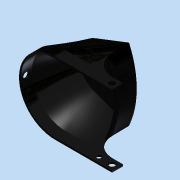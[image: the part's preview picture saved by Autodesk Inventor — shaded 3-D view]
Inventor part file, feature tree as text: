
AUTODESK INVENTOR PART (.ipt)
format: ipt  version: 2015 (Build 190159000, 159)  size: 537,600 bytes
history: native  units: in
note: dims shown in document units (in); Inventor stores cm internally (conversion verified against a paired STEP export)
features: sketch x11, extrude x8, other x4, plane x3, mirror x2, projected_geometry x2, loft x1, sweep x1
ambient origin geometry x8: Origin, YZ Plane, XZ Plane, XY Plane, X Axis, Y Axis, Z Axis, Center Point
bodies: Solid1 (feature_tree)
feature tree (32):
  other  "MotorMount.ipt"
  sketch  "Sketch2"  dims[d0=0.3937in d1=1.3189in]
  sketch  "Sketch3"  dims[d2=1.5748in d3=0.0625in]
  plane  "Work Plane1"
  loft  "Loft1"
  extrude  "Extrusion1"  Depth=0.0625in
  extrude  "Extrusion2"  TaperAngle=0.0deg  [1 undecoded]
  sketch  "Sketch6"  dims[d10=0.0in d11=0.0625in]
  extrude  "Extrusion3"  Depth=0.0625in
  plane  "Work Plane2"
  extrude  "Extrusion4"  Depth=0.0625in
  sketch  "Sketch8"  dims[d14=0.0625in d15=0.0in]
  extrude  "Extrusion5"  TaperAngle=0.0deg  [1 undecoded]
  extrude  "Extrusion6"  TaperAngle=0.0deg  [1 undecoded]
  plane  "Work Plane3"
  mirror  "Mirror1"
  extrude  "Extrusion7"  TaperAngle=0.0deg  [1 undecoded]
  mirror  "Mirror2"
  sketch  "Sketch10"  dims[d18=0.1339in d19=0.1339in]
  sweep  "Sweep2"
  extrude  "Extrusion8"  Depth=0.1339in
  other  "TaggingFeature1"
  sketch  "Sketch4"  dims[d4=0.0625in d5=0.0in d6=90.0deg]
  sketch  "Sketch5"  dims[d7=0.0in d8=90.0deg d9=0.0625in]
  sketch  "Sketch7"  dims[d12=0.0625in d13=0.0in]
  sketch  "Sketch9"  dims[d16=0.0625in d17=0.0in]
  projected_geometry  "Projected Loop1"
  projected_geometry  "Projected Loop2"
  sketch  "Sketch11"  dims[d20=0.1339in d21=0.1339in d22=0.1969in d23=0.1969in d24=0.1969in d25=0.1969in d26=0.1412in d27=0.0in d28=0.0625in d29=0.0in d31=0.75in d32=0.0625in d33=0.0in d34=0.96in d35=0.96in d36=0.0625in d39=0.0in d40=0.0in d41=0.5in d42=0.0in d44=0.205in d45=0.205in d46=0.1575in]
  sketch  "3D Sketch2"
  other  "Solid2::MotorMount.ipt"
  other  "Srf1"
note: 4 required parameter values undecoded (feature->parameter linkage not recoverable at this tier; creation-order binding heuristic only, values carry confidence <= 0.55)
